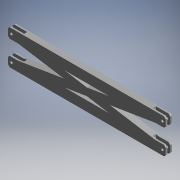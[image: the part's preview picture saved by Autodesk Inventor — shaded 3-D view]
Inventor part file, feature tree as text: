
AUTODESK INVENTOR PART (.ipt)
format: ipt  version: 2019 (Build 230136000, 136)  size: 343,552 bytes
history: native  units: mm (DEFAULTED — no unit token found)
features: extrude x2, sketch x1, projected_geometry x1
ambient origin geometry x8: Origin, YZ Plane, XZ Plane, XY Plane, X Axis, Y Axis, Z Axis, Center Point
bodies: Body1 (feature_tree)
feature tree (4):
  extrude  "Extrusion2"  Depth=2.0mm
  extrude  "Extrusion3"  Depth=2.0mm
  sketch  "Sketch2"  dims[d0=3.0mm d1=3.0mm d2=183.0mm d4=4.0mm d10=2.0mm d11=2.0mm d12=2.0mm d13=2.0mm d14=2.0mm d15=2.0mm d16=2.0mm d17=2.0mm d18=30.0mm d19=9.0mm d20=12.0mm d21=12.0mm d22=12.0mm d23=10.5mm d24=10.5mm d25=9.0mm d26=9.0mm d27=9.0mm d28=9.0mm d29=12.0mm d30=7.6mm d31=0.0mm d32=3.6mm d33=17.5mm d34=2.0mm d35=0.0mm]
  projected_geometry  "Projected Loop1"
